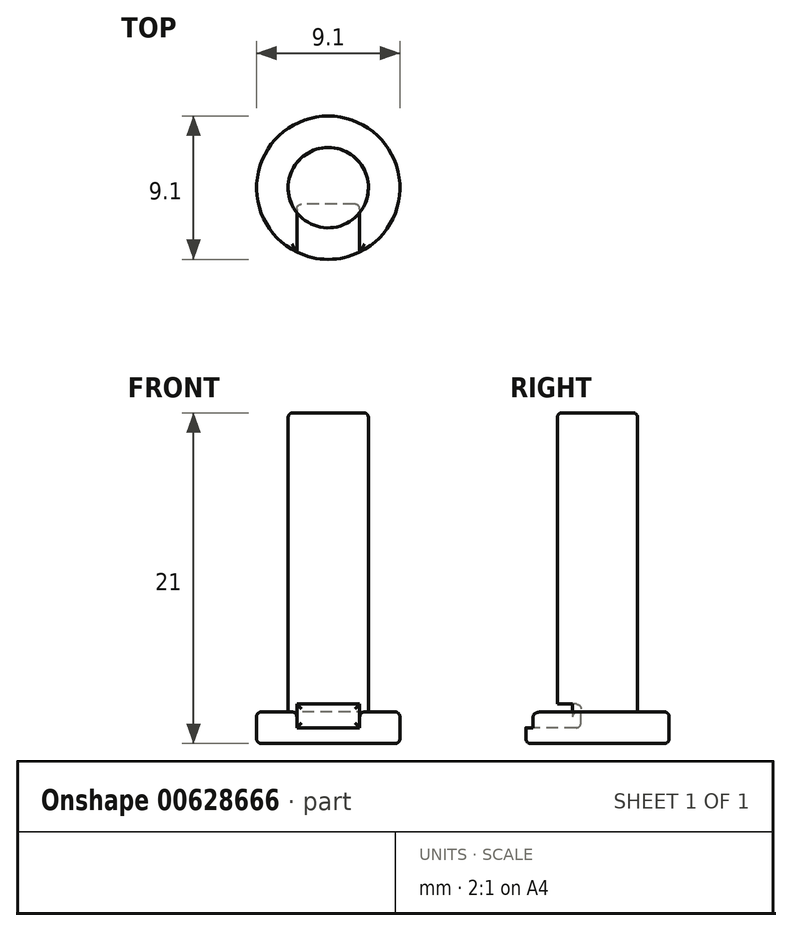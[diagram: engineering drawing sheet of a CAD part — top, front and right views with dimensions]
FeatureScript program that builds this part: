
annotation { "Feature Type Name" : "Feature", "Feature Type Description" : "" }
export const myFeature = defineFeature(function(context is Context, id is Id, definition is map)
    precondition{}
    {
        {
            var Q0;
            Q0=qCreatedBy(makeId("Top.planeOp"),FACE);
            var sketch = newSketch(context, id + "F0", { "sketchPlane" : qUnion([Q0])});
            skCircle(sketch, "E0", {"center": v(0, 0) * mm, "radius": 2.55 * mm});
            skCircle(sketch, "E1", {"center": v(0, 0) * mm, "radius": 4.55 * mm});
            skSolve(sketch);
        }
        {
            var Q0;
            Q0=makeQuery(id+"F0.imprint","IMPRINT",FACE,{"disambiguationData":[TD([[makeQuery(id+"F0.imprint","IMPRINT",EDGE,{"derivedFrom":sQuery(id+"F0.wireOp",EDGE,"E0")}),-1.0]])]});
            extrude(context, id + "F1", {"entities" : qUnion([Q0]), "depth" : 2 * mm, "offsetDistance" : 25 * mm});
        }
        {
            var Q0;
            Q0=makeQuery(id+"F0.imprint","IMPRINT",FACE,{"disambiguationData":[TD([[makeQuery(id+"F0.imprint","IMPRINT",EDGE,{"derivedFrom":sQuery(id+"F0.wireOp",EDGE,"E0")}),1.0]])]});
            extrude(context, id + "F2", {"entities" : qUnion([Q0]), "operationType" : NewBodyOperationType.ADD, "depth" : (19 + 2) * mm, "offsetDistance" : 25 * mm});
        }
        {
            var Q0;
            Q0=makeQuery(id+"F1.opExtrude","CAP_FACE",FACE,{"disambiguationData":[OSD([sQuery(id+"F0.wireOp",EDGE,"E0"),sQuery(id+"F0.wireOp",EDGE,"E1")])],"isStart":false});
            var sketch = newSketch(context, id + "F3", { "sketchPlane" : qUnion([Q0])});
            skLineSegment(sketch, "E2", {"start": v(0, 0) * mm, "end": v(0, -2.55) * mm, "construction": true});
            skLineSegment(sketch, "E3", {"start": v(0, -2.55) * mm, "end": v(0, -4.55) * mm, "construction": true});
            skLineSegment(sketch, "E4.bottom", {"start": v(2, -1.05) * mm, "end": v(-2, -1.05) * mm});
            skLineSegment(sketch, "E4.top", {"start": v(2, -6.05) * mm, "end": v(-2, -6.05) * mm});
            skLineSegment(sketch, "E4.left", {"start": v(2, -1.05) * mm, "end": v(2, -6.05) * mm});
            skLineSegment(sketch, "E4.right", {"start": v(-2, -1.05) * mm, "end": v(-2, -6.05) * mm});
            skPoint(sketch, "E4.middle", {"position": v(0, -3.55) * mm});
            skSolve(sketch);
        }
        {
            var Q0;
            {var subQ0=sQuery(id+"F3.wireOp",EDGE,"E4.top");Q0=makeQuery(id+"F3.imprint","IMPRINT",FACE,{"disambiguationData":[TD([[makeQuery(id+"F3.imprint","IMPRINT",EDGE,{"derivedFrom":subQ0}),-1.0]])]});}
            var Q1;
            {var subQ0=sQuery(id+"F3.wireOp",EDGE,"E4.left");var subQ1=makeQuery(id+"F1.opExtrude","CAP_EDGE",EDGE,{"disambiguationData":[OSD([sQuery(id+"F0.wireOp",EDGE,"E1")])],"isStart":false});var subQ2=makeQuery(id+"F3.imprint","INTERSECT",VERTEX,{"derivedFrom":[subQ1,subQ0]});Q1=makeQuery(id+"F3.imprint","IMPRINT",FACE,{"disambiguationData":[TD([[makeQuery(id+"F3.imprint","IMPRINT",EDGE,{"disambiguationData":[TD([[subQ2,1.0]])],"derivedFrom":subQ0}),-1.0]])]});}
            var Q2;
            {var subQ0=sQuery(id+"F3.wireOp",EDGE,"E4.bottom");Q2=makeQuery(id+"F3.imprint","IMPRINT",FACE,{"disambiguationData":[TD([[makeQuery(id+"F3.imprint","IMPRINT",EDGE,{"derivedFrom":subQ0}),1.0]])]});}
            extrude(context, id + "F4", {"entities" : qUnion([Q0, Q1, Q2]), "operationType" : NewBodyOperationType.REMOVE, "oppositeDirection" : true, "depth" : 1 * mm, "offsetDistance" : 25 * mm, "hasSecondDirection" : true, "secondDirectionOppositeDirection" : false, "secondDirectionDepth" : 0.5 * mm});
        }
        {
            var Q0;
            {var subQ0=sQuery(id+"F0.wireOp",EDGE,"E0");Q0=makeQuery(id+"F2.boolean.opBoolean","MERGE",FACE,{"derivedFrom":[makeQuery(id+"F1.opExtrude","CAP_FACE",FACE,{"disambiguationData":[OSD([subQ0,sQuery(id+"F0.wireOp",EDGE,"E1")])],"isStart":true}),makeQuery(id+"F2.opExtrude","CAP_FACE",FACE,{"disambiguationData":[OSD([subQ0])],"isStart":true})]});}
            var Q1;
            Q1=makeQuery(id+"F2.opExtrude","CAP_FACE",FACE,{"disambiguationData":[OSD([sQuery(id+"F0.wireOp",EDGE,"E0")])],"isStart":false});
            var Q2;
            Q2=makeQuery(id+"F1.opExtrude","CAP_EDGE",EDGE,{"disambiguationData":[OSD([sQuery(id+"F0.wireOp",EDGE,"E1")])],"isStart":false});
            var Q3;
            Q3=makeQuery(id+"F4.boolean.opBoolean","COPY",EDGE,{"derivedFrom":makeQuery(id+"F4.opExtrude","CAP_EDGE",EDGE,{"disambiguationData":[OSD([sQuery(id+"F3.wireOp",EDGE,"E4.bottom")])],"isStart":false})});
            var Q4;
            Q4=makeQuery(id+"F4.boolean.opBoolean","COPY",EDGE,{"derivedFrom":makeQuery(id+"F4.opExtrude","CAP_EDGE",EDGE,{"disambiguationData":[OSD([sQuery(id+"F3.wireOp",EDGE,"E4.bottom")])],"isStart":true})});
            var Q5;
            Q5=makeQuery(id+"F4.boolean.opBoolean","COPY",EDGE,{"derivedFrom":makeQuery(id+"F4.opExtrude","SWEPT_EDGE",EDGE,{"disambiguationData":[OSD([sQuery(id+"F3.wireOp",EDGE,"E4.bottom"),sQuery(id+"F3.wireOp",EDGE,"E4.left")])]})});
            var Q6;
            Q6=makeQuery(id+"F4.boolean.opBoolean","COPY",EDGE,{"derivedFrom":makeQuery(id+"F4.opExtrude","SWEPT_EDGE",EDGE,{"disambiguationData":[OSD([sQuery(id+"F3.wireOp",EDGE,"E4.bottom"),sQuery(id+"F3.wireOp",EDGE,"E4.right")])]})});
            var Q7;
            Q7=makeQuery(id+"F4.boolean.opBoolean","INTERSECT",EDGE,{"derivedFrom":[makeQuery(id+"F1.opExtrude","CAP_FACE",FACE,{"disambiguationData":[OSD([sQuery(id+"F0.wireOp",EDGE,"E0"),sQuery(id+"F0.wireOp",EDGE,"E1")])],"isStart":false}),makeQuery(id+"F4.opExtrude","SWEPT_FACE",FACE,{"disambiguationData":[OSD([sQuery(id+"F3.wireOp",EDGE,"E4.right")])]})]});
            var Q8;
            Q8=makeQuery(id+"F4.boolean.opBoolean","INTERSECT",EDGE,{"derivedFrom":[makeQuery(id+"F1.opExtrude","CAP_FACE",FACE,{"disambiguationData":[OSD([sQuery(id+"F0.wireOp",EDGE,"E0"),sQuery(id+"F0.wireOp",EDGE,"E1")])],"isStart":false}),makeQuery(id+"F4.opExtrude","SWEPT_FACE",FACE,{"disambiguationData":[OSD([sQuery(id+"F3.wireOp",EDGE,"E4.left")])]})]});
            fillet(context, id + "F5", {"entities" : qUnion([Q0, Q1, Q2, Q3, Q4, Q5, Q6, Q7, Q8]), "radius" : 0.3 * mm, "tangentPropagation" : true, "allowEdgeOverflow" : false});
        }
    });
